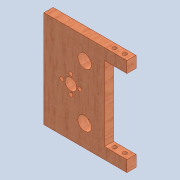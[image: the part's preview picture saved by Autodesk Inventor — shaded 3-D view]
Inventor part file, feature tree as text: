
AUTODESK INVENTOR PART (.ipt)
format: ipt  version: 2020 (Build 240168000, 168)  size: 297,472 bytes
history: native  units: mm
features: sketch x5, extrude x4, other x2, hole x1, reference x1
ambient origin geometry x8: Origin, YZ Plane, XZ Plane, XY Plane, X Axis, Y Axis, Z Axis, Center Point
bodies: Solid1 (feature_tree)
feature tree (13):
  extrude  "Extrusion1"  Depth=86.0mm
  extrude  "Extrusion4"  Depth=20.0mm
  extrude  "Extrusion5"  Depth=10.0mm TaperAngle=0.0deg
  extrude  "Extrusion6"  Depth=10.0mm TaperAngle=0.0deg
  hole  "Hole1"  [1 undecoded]
  sketch  "Sketch1"  dims[d0=73.5mm d1=86.0mm]
  sketch  "Sketch4"  dims[d2=8.0mm d3=0.0mm d19=20.0mm]
  sketch  "Sketch5"  dims[d20=66.0mm d21=10.0mm d22=0.0mm]
  reference  "Reference1"
  sketch  "Sketch6"  dims[d23=12.0mm d29=10.0mm d30=0.0mm]
  sketch  "Sketch7"  dims[d37=37.5mm d38=19.0mm d39=19.0mm d40=10.0mm d41=0.0mm d42=3.5mm d43=10.2mm d44=23.751158mm d46=22.0mm d47=16.0mm d48=9.0mm d49=6.0mm d50=3.5mm d51=6.0mm d52=4.0mm d53=2.0mm d54=90.0deg d55=8.0mm d56=20.594885mm]
  other  "0005-10-04 Y axis and extruder.iam"
  other  "0005-10-009.ipt:14"
note: 1 required parameter value undecoded (feature->parameter linkage not recoverable at this tier; creation-order binding heuristic only, values carry confidence <= 0.55)
